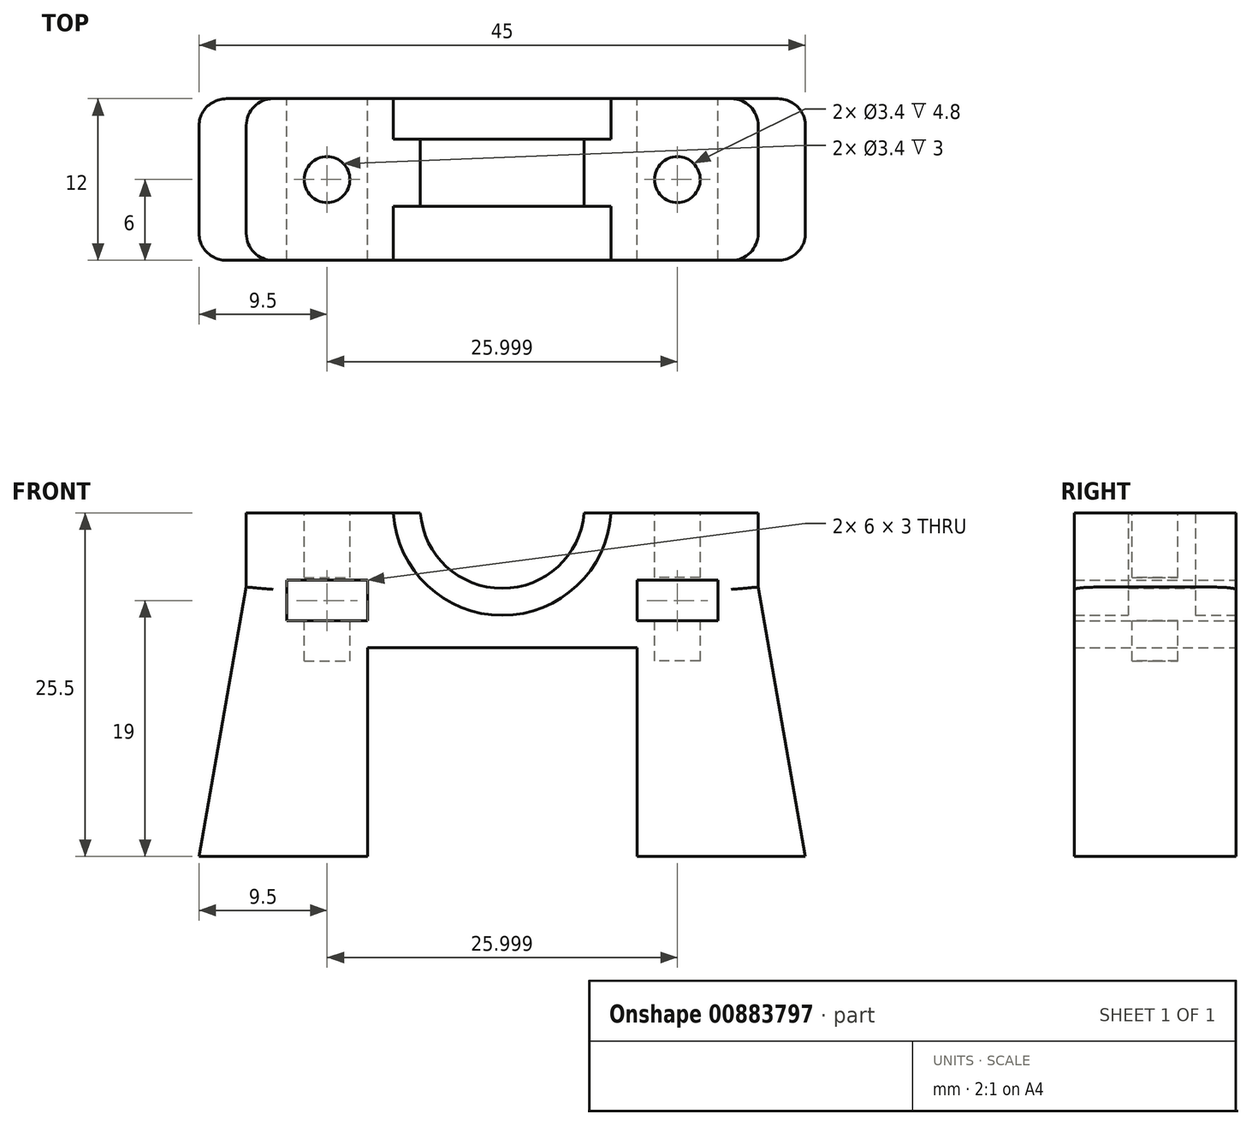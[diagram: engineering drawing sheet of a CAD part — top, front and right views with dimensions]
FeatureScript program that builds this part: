
annotation { "Feature Type Name" : "Feature", "Feature Type Description" : "" }
export const myFeature = defineFeature(function(context is Context, id is Id, definition is map)
    precondition{}
    {
        {
            var Q0;
            Q0=qCreatedBy(makeId("Front.planeOp"),FACE);
            var sketch = newSketch(context, id + "F0", { "sketchPlane" : qUnion([Q0])});
            skLineSegment(sketch, "E0", {"start": v(22.5, 0) * mm, "end": v(10, 0) * mm});
            skLineSegment(sketch, "E1", {"start": v(22.5, 0) * mm, "end": v(0, 0) * mm, "construction": true});
            skLineSegment(sketch, "E2.MirrorCS", {"start": v(16, 17.5) * mm, "end": v(16, 20.5) * mm});
            skLineSegment(sketch, "E3.MirrorCS", {"start": v(0, 19.9) * mm, "end": v(0, 15.5) * mm});
            skLineSegment(sketch, "E4.MirrorCS", {"start": v(10, 17.5) * mm, "end": v(10, 20.5) * mm});
            skLineSegment(sketch, "E5.MirrorCS", {"start": v(16, 20.5) * mm, "end": v(10, 20.5) * mm});
            skLineSegment(sketch, "E6.MirrorCS", {"start": v(19, 20) * mm, "end": v(19, 25.5) * mm});
            skLineSegment(sketch, "E7.MirrorCS", {"start": v(10, 17.5) * mm, "end": v(16, 17.5) * mm});
            skLineSegment(sketch, "E8.MirrorCS", {"start": v(22.5, 0) * mm, "end": v(19, 20) * mm});
            skLineSegment(sketch, "E9.MirrorCS", {"start": v(10, 15.5) * mm, "end": v(0, 15.5) * mm});
            skLineSegment(sketch, "E10.MirrorCS", {"start": v(10, 0) * mm, "end": v(10, 15.5) * mm});
            skArc(sketch, "E11.MirrorCS", {"start": v(0, 19.9) * mm, "mid": v(4.13, 21.51) * mm, "end": v(6.08, 25.5) * mm});
            skLineSegment(sketch, "E12.MirrorCS", {"start": v(19, 25.5) * mm, "end": v(6.08, 25.5) * mm});
            skArc(sketch, "E13.MirrorCS", {"start": v(0, 17.9) * mm, "mid": v(5.55, 20.1) * mm, "end": v(8.08, 25.5) * mm});
            skLineSegment(sketch, "E14", {"start": v(0, 31) * mm, "end": v(0, 0) * mm, "construction": true});
            skSolve(sketch);
        }
        {
            var Q0;
            Q0=makeQuery(id+"F0.imprint","IMPRINT",FACE,{"disambiguationData":[TD([[makeQuery(id+"F0.imprint","IMPRINT",EDGE,{"derivedFrom":sQuery(id+"F0.wireOp",EDGE,"E0")}),-1.0]])]});
            extrude(context, id + "F1", {"entities" : qUnion([Q0]), "depth" : 12 * mm, "offsetDistance" : 25 * mm, "symmetric" : true});
        }
        {
            var Q0;
            {var subQ0=sQuery(id+"F0.wireOp",EDGE,"E11.MirrorCS");Q0=makeQuery(id+"F0.imprint","IMPRINT",FACE,{"disambiguationData":[TD([[makeQuery(id+"F0.imprint","IMPRINT",EDGE,{"derivedFrom":subQ0}),-1.0]])]});}
            extrude(context, id + "F2", {"entities" : qUnion([Q0]), "operationType" : NewBodyOperationType.ADD, "depth" : 2 * mm, "offsetDistance" : 25 * mm, "hasSecondDirection" : true, "secondDirectionOppositeDirection" : true, "secondDirectionDepth" : 3 * mm});
        }
        {
            var Q0;
            {var subQ0=sQuery(id+"F0.wireOp",EDGE,"E12.MirrorCS");Q0=makeQuery(id+"F2.boolean.opBoolean","MERGE",FACE,{"derivedFrom":[makeQuery(id+"F1.opExtrude","SWEPT_FACE",FACE,{"disambiguationData":[OSD([subQ0])]}),makeQuery(id+"F2.opExtrude","SWEPT_FACE",FACE,{"disambiguationData":[OSD([subQ0])]})]});}
            var sketch = newSketch(context, id + "F3", { "sketchPlane" : qUnion([Q0])});
            skCircle(sketch, "E15", {"center": v(13, 0) * mm, "radius": 1.7 * mm});
            skSolve(sketch);
        }
        {
            var Q0;
            Q0=makeQuery(id+"F3.imprint","IMPRINT",FACE,{"disambiguationData":[TD([[makeQuery(id+"F3.imprint","IMPRINT",EDGE,{"derivedFrom":sQuery(id+"F3.wireOp",EDGE,"E15")}),1.0]])]});
            extrude(context, id + "F4", {"entities" : qUnion([Q0]), "operationType" : NewBodyOperationType.REMOVE, "oppositeDirection" : true, "depth" : 4.8 * mm, "offsetDistance" : 25 * mm});
        }
        {
            var Q0;
            Q0=makeQuery(id+"F1.opExtrude","CAP_EDGE",EDGE,{"disambiguationData":[OSD([sQuery(id+"F0.wireOp",EDGE,"E8.MirrorCS")])],"isStart":true});
            var Q1;
            Q1=makeQuery(id+"F1.opExtrude","CAP_EDGE",EDGE,{"disambiguationData":[OSD([sQuery(id+"F0.wireOp",EDGE,"E6.MirrorCS")])],"isStart":true});
            var Q2;
            Q2=makeQuery(id+"F1.opExtrude","CAP_EDGE",EDGE,{"disambiguationData":[OSD([sQuery(id+"F0.wireOp",EDGE,"E8.MirrorCS")])],"isStart":false});
            var Q3;
            Q3=makeQuery(id+"F1.opExtrude","CAP_EDGE",EDGE,{"disambiguationData":[OSD([sQuery(id+"F0.wireOp",EDGE,"E6.MirrorCS")])],"isStart":false});
            fillet(context, id + "F5", {"entities" : qUnion([Q0, Q1, Q2, Q3]), "radius" : 2 * mm, "tangentPropagation" : true, "allowEdgeOverflow" : false});
        }
        {
            var Q0;
            Q0=makeQuery(id+"F1.opExtrude","SWEPT_FACE",FACE,{"disambiguationData":[OSD([sQuery(id+"F0.wireOp",EDGE,"E7.MirrorCS")])]});
            var sketch = newSketch(context, id + "F6", { "sketchPlane" : qUnion([Q0])});
            skCircle(sketch, "E16", {"center": v(13, 0) * mm, "radius": 1.7 * mm});
            skPoint(sketch, "E16.centerSnap0", {"position": v(13, 6) * mm});
            skSolve(sketch);
        }
        {
            var Q0;
            Q0=makeQuery(id+"F6.imprint","IMPRINT",FACE,{"disambiguationData":[TD([[makeQuery(id+"F6.imprint","IMPRINT",EDGE,{"derivedFrom":sQuery(id+"F6.wireOp",EDGE,"E16")}),1.0]])]});
            extrude(context, id + "F7", {"entities" : qUnion([Q0]), "operationType" : NewBodyOperationType.REMOVE, "oppositeDirection" : true, "depth" : 3 * mm, "offsetDistance" : 25 * mm});
        }
        {
            var Q0;
            Q0=makeQuery(id+"F1.opExtrude","SWEPT_BODY",BODY,{"disambiguationData":[OSD([sQuery(id+"F0.wireOp",EDGE,"E0"),sQuery(id+"F0.wireOp",EDGE,"E2.MirrorCS"),sQuery(id+"F0.wireOp",EDGE,"E3.MirrorCS"),sQuery(id+"F0.wireOp",EDGE,"E4.MirrorCS"),sQuery(id+"F0.wireOp",EDGE,"E5.MirrorCS"),sQuery(id+"F0.wireOp",EDGE,"E6.MirrorCS"),sQuery(id+"F0.wireOp",EDGE,"E7.MirrorCS"),sQuery(id+"F0.wireOp",EDGE,"E8.MirrorCS"),sQuery(id+"F0.wireOp",EDGE,"E9.MirrorCS"),sQuery(id+"F0.wireOp",EDGE,"E10.MirrorCS"),sQuery(id+"F0.wireOp",EDGE,"E12.MirrorCS"),sQuery(id+"F0.wireOp",EDGE,"E13.MirrorCS")])]});
            var Q1;
            Q1=qCreatedBy(makeId("Right.planeOp"),FACE);
            mirror(context, id + "F8", {"operationType" : NewBodyOperationType.ADD, "entities" : qUnion([Q0]), "mirrorPlane" : qUnion([Q1])});
        }
    });
